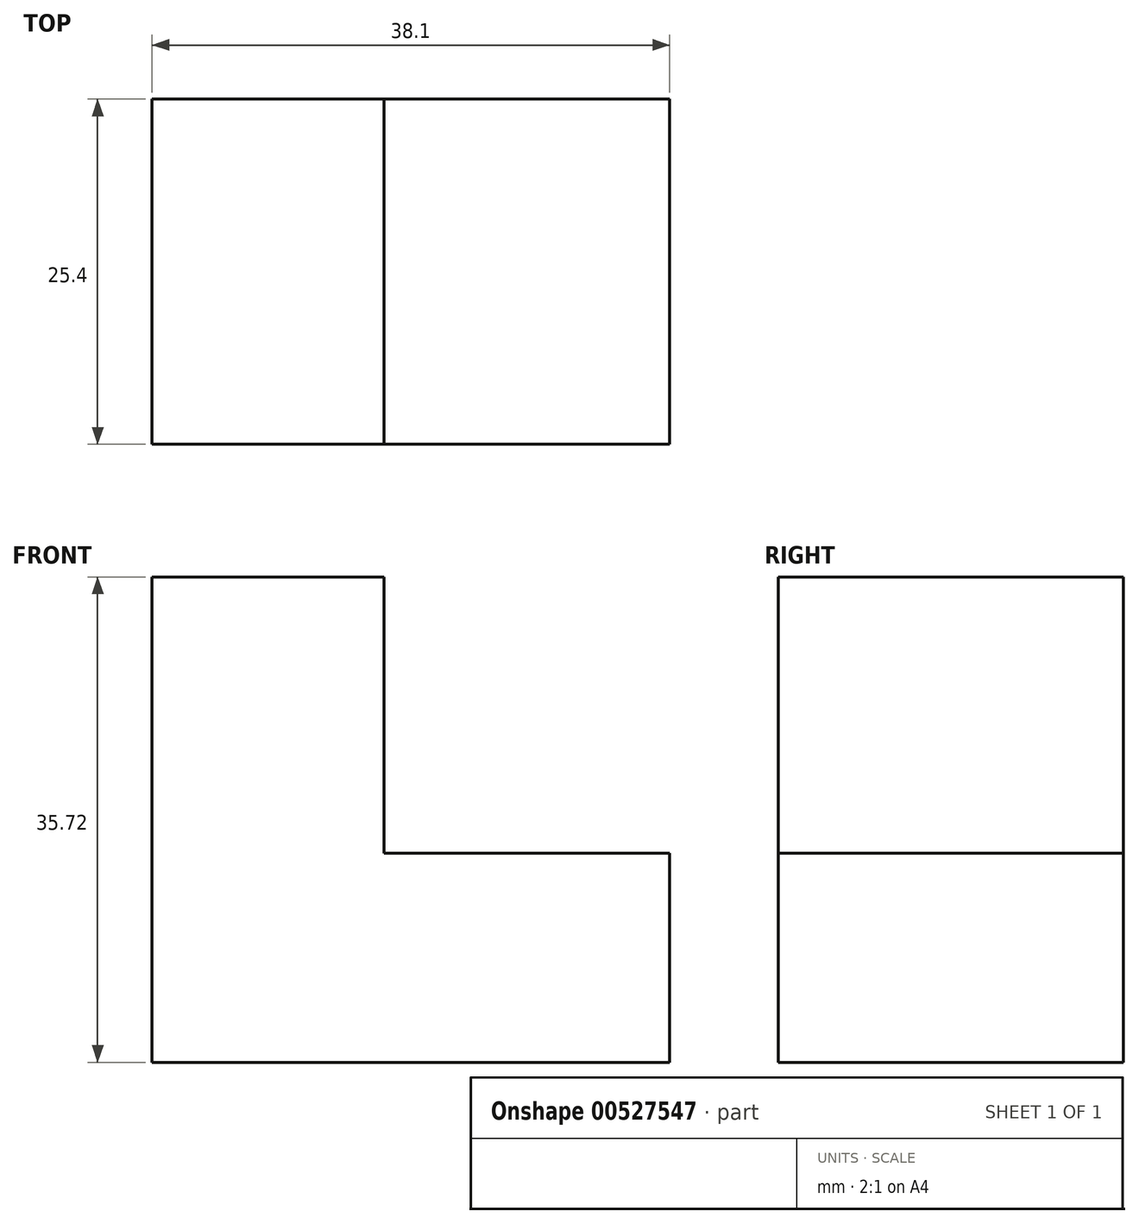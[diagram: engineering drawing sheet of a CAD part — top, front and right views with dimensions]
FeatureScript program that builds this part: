
annotation { "Feature Type Name" : "Feature", "Feature Type Description" : "" }
export const myFeature = defineFeature(function(context is Context, id is Id, definition is map)
    precondition{}
    {
        {
            var Q0;
            Q0=qCreatedBy(makeId("Front.planeOp"),FACE);
            var sketch = newSketch(context, id + "F0", { "sketchPlane" : qUnion([Q0])});
            skLineSegment(sketch, "E0", {"start": v(0, 0) * mm, "end": v(0, 35.72) * mm});
            skLineSegment(sketch, "E1", {"start": v(0, 35.72) * mm, "end": v(17.07, 35.72) * mm});
            skLineSegment(sketch, "E2", {"start": v(17.07, 35.72) * mm, "end": v(17.07, 15.4) * mm});
            skLineSegment(sketch, "E3", {"start": v(17.07, 15.4) * mm, "end": v(38.1, 15.4) * mm});
            skLineSegment(sketch, "E4", {"start": v(38.1, 15.4) * mm, "end": v(38.1, 0) * mm});
            skLineSegment(sketch, "E5", {"start": v(0, 0) * mm, "end": v(38.1, 0) * mm});
            skSolve(sketch);
        }
        {
            var Q0;
            Q0=makeQuery(id+"F0.imprint","IMPRINT",FACE,{"disambiguationData":[TD([[makeQuery(id+"F0.imprint","IMPRINT",EDGE,{"derivedFrom":sQuery(id+"F0.wireOp",EDGE,"E0")}),-1.0]])]});
            extrude(context, id + "F1", {"entities" : qUnion([Q0]), "depth" : 25.4 * mm, "offsetDistance" : 25.4 * mm});
        }
    });
